# Revit family: Stair_Modular_Kattsafe_Platform_LeftExit
name_source: partatom
category: Specialty Equipment
units: mm (PartAtom-declared; Revit-internal decimal feet)

## family parameters
Always vertical = Yes
Cut with Voids When Loaded = No
Enable Cutting in Views = No
Maintain Annotation Orientation = No
OmniClass Number = 23.17.23.17
Part Type = Normal
Room Calculation Point = No
Round Connector Dimension = Use Diameter
Shared = No
Work Plane-Based = No

## types (1)
- 600 Series
    Assembly Code = E1090100
    Default Elevation = 0 mm  [stored 0 ft]
    Description = Kattsafe platforms and stairs are pre-engineered aluminum for a no-weld, modular access system. All systems offer flexible height access and fall protection solutions with a modular design for simplified installation and on-site flexibility.
    ElementType = Stair
    Export Type to IFC As = IfcStair
    IfcExportAs = IfcStair
    IfcExportType = STRAIGHT_RUN_STAIR
    Manufacturer = Kattsafe®
    ManufacturerSpecCode = KS30L
    ManufacturerURLProductSpecific = https://kattsafe.com.au
    Model = KS30L
    ModifiedIssue = 20240430 $
    StairType = 600 Series
    StairTypeSelector = 1
    StairWidth = 610 mm  [stored 2.00131 ft]
    Type Comments = 600 Series, 674 Stairs Width
    Type IFC Predefined Type = STRAIGHT_RUN_STAIR
    URL = https://kattsafe.com.au
    Uniclass2015Code = Pr_25_30_85
    Uniclass2015Title = Stair and ladder units
    Uniclass2015Version = Products v1.23

note: [stored X ft] marks values corroborated as IEEE doubles in the binary element streams (Revit-internal decimal feet)

## geometry (parser evidence)
native form markers: Sweep x40
no freeform markers — native parametric forms only
